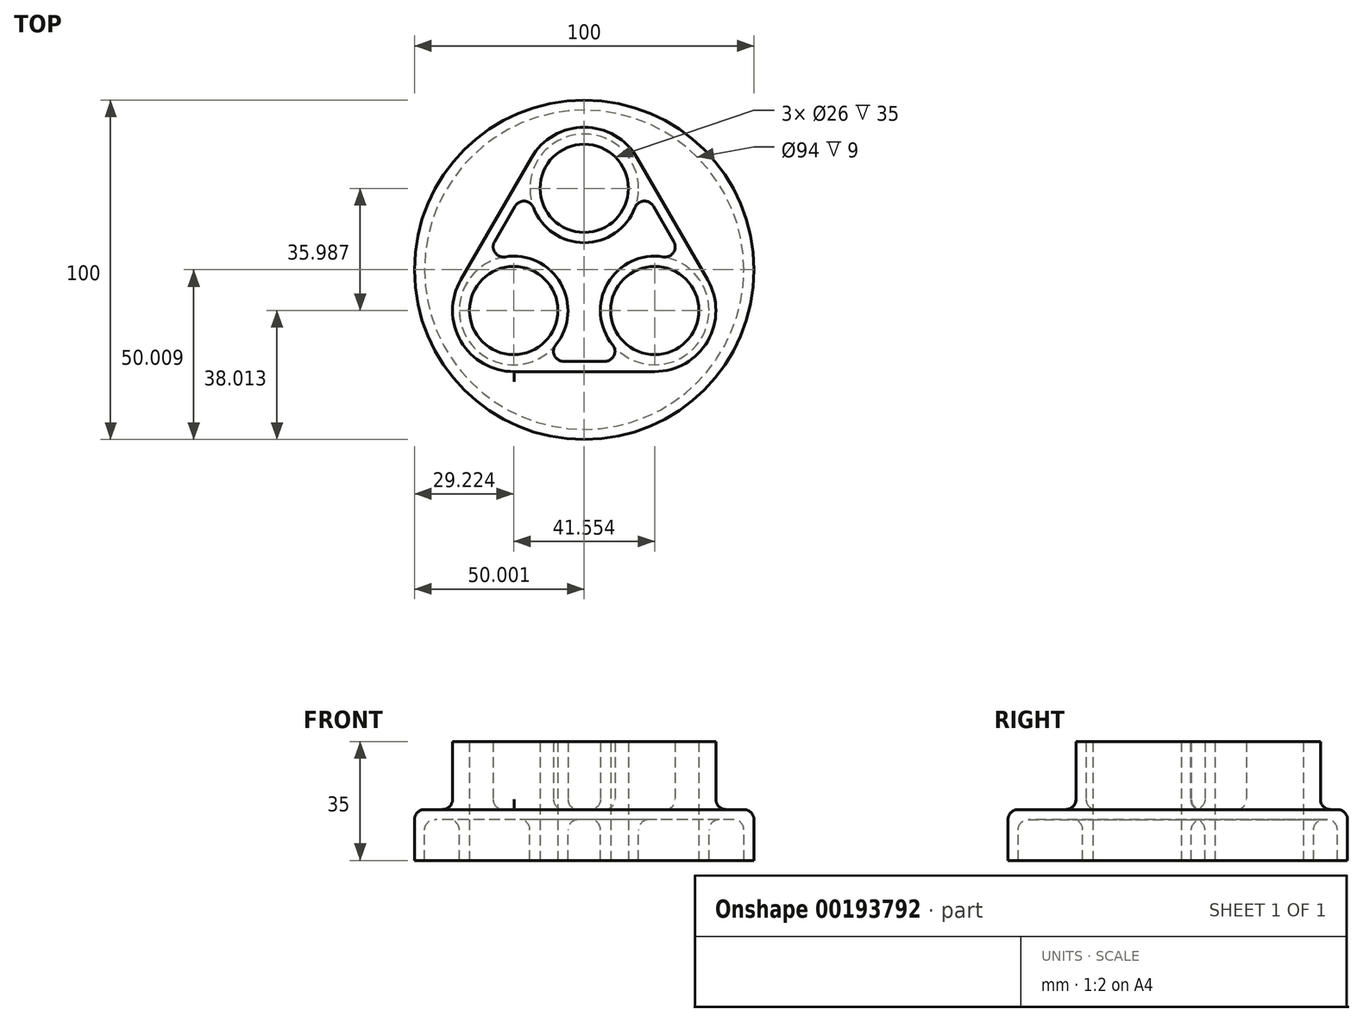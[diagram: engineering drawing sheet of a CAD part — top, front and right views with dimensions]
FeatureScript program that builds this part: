
annotation { "Feature Type Name" : "Feature", "Feature Type Description" : "" }
export const myFeature = defineFeature(function(context is Context, id is Id, definition is map)
    precondition{}
    {
        {
            var Q0;
            Q0=qCreatedBy(makeId("Top.planeOp"),FACE);
            var sketch = newSketch(context, id + "F0", { "sketchPlane" : qUnion([Q0])});
            skCircle(sketch, "E0", {"center": v(0, 0) * mm, "radius": 24 * mm, "construction": true});
            skCircle(sketch, "E1", {"center": v(0, 24) * mm, "radius": 13 * mm});
            skCircle(sketch, "E2", {"center": v(0, 24) * mm, "radius": 18 * mm});
            skCircle(sketch, "E3.1.0", {"center": v(-20.78, -11.99) * mm, "radius": 18 * mm});
            skCircle(sketch, "E3.1.1", {"center": v(-20.78, -11.99) * mm, "radius": 13 * mm});
            skCircle(sketch, "E3.2.0", {"center": v(20.78, -11.99) * mm, "radius": 18 * mm});
            skCircle(sketch, "E3.2.1", {"center": v(20.78, -11.99) * mm, "radius": 13 * mm});
            skCircle(sketch, "E4", {"center": v(0, 0) * mm, "radius": 50 * mm});
            skLineSegment(sketch, "E5", {"start": v(-15.59, 33) * mm, "end": v(-36.36, -2.99) * mm});
            skLineSegment(sketch, "E6", {"start": v(15.59, 33) * mm, "end": v(36.37, -2.99) * mm});
            skLineSegment(sketch, "E7", {"start": v(-15.2, -26.99) * mm, "end": v(15.2, -26.99) * mm});
            skLineSegment(sketch, "E8", {"start": v(30.98, 0.34) * mm, "end": v(15.77, 26.68) * mm});
            skLineSegment(sketch, "E9", {"start": v(-15.77, 26.68) * mm, "end": v(-30.98, 0.33) * mm});
            skLineSegment(sketch, "E10", {"start": v(-20.6, -29.99) * mm, "end": v(20.78, -29.99) * mm});
            skCircle(sketch, "E11", {"center": v(0, 24) * mm, "radius": 16 * mm});
            skCircle(sketch, "E12", {"center": v(20.78, -11.99) * mm, "radius": 16 * mm});
            skCircle(sketch, "E13", {"center": v(-20.78, -11.99) * mm, "radius": 16 * mm});
            skCircle(sketch, "E14", {"center": v(0, 0) * mm, "radius": 47 * mm});
            skSolve(sketch);
        }
        {
            var Q0;
            {var subQ0=sQuery(id+"F0.wireOp",EDGE,"E7");Q0=makeQuery(id+"F0.imprint","IMPRINT",FACE,{"disambiguationData":[TD([[makeQuery(id+"F0.imprint","IMPRINT",EDGE,{"derivedFrom":subQ0}),-1.0]])]});}
            var Q1;
            Q1=makeQuery(id+"F0.imprint","IMPRINT",FACE,{"disambiguationData":[TD([[makeQuery(id+"F0.imprint","IMPRINT",EDGE,{"derivedFrom":sQuery(id+"F0.wireOp",EDGE,"E3.2.1")}),-1.0]])]});
            var Q2;
            Q2=makeQuery(id+"F0.imprint","IMPRINT",FACE,{"disambiguationData":[TD([[makeQuery(id+"F0.imprint","IMPRINT",EDGE,{"derivedFrom":sQuery(id+"F0.wireOp",EDGE,"E3.1.1")}),-1.0]])]});
            var Q3;
            Q3=makeQuery(id+"F0.imprint","IMPRINT",FACE,{"disambiguationData":[TD([[makeQuery(id+"F0.imprint","IMPRINT",EDGE,{"derivedFrom":sQuery(id+"F0.wireOp",EDGE,"E1")}),-1.0]])]});
            var Q4;
            {var subQ0=sQuery(id+"F0.wireOp",EDGE,"E6");Q4=makeQuery(id+"F0.imprint","IMPRINT",FACE,{"disambiguationData":[TD([[makeQuery(id+"F0.imprint","IMPRINT",EDGE,{"derivedFrom":subQ0}),-1.0]])]});}
            var Q5;
            {var subQ0=sQuery(id+"F0.wireOp",EDGE,"E5");Q5=makeQuery(id+"F0.imprint","IMPRINT",FACE,{"disambiguationData":[TD([[makeQuery(id+"F0.imprint","IMPRINT",EDGE,{"derivedFrom":subQ0}),1.0]])]});}
            var Q6;
            {var subQ3=sQuery(id+"F0.wireOp",EDGE,"E3.1.0");var subQ5=makeQuery(id+"F0.imprint","INTERSECT",VERTEX,{"derivedFrom":[subQ3,sQuery(id+"F0.wireOp",EDGE,"E5")]});Q6=makeQuery(id+"F0.imprint","IMPRINT",FACE,{"disambiguationData":[TD([[makeQuery(id+"F0.imprint","IMPRINT",EDGE,{"disambiguationData":[TD([[subQ5,-1.0]])],"derivedFrom":subQ3}),1.0]])]});}
            var Q7;
            {var subQ0=sQuery(id+"F0.wireOp",EDGE,"E2");var subQ6=makeQuery(id+"F0.imprint","INTERSECT",VERTEX,{"derivedFrom":[subQ0,sQuery(id+"F0.wireOp",EDGE,"E5")]});Q7=makeQuery(id+"F0.imprint","IMPRINT",FACE,{"disambiguationData":[TD([[makeQuery(id+"F0.imprint","IMPRINT",EDGE,{"disambiguationData":[TD([[subQ6,1.0]])],"derivedFrom":subQ0}),1.0]])]});}
            var Q8;
            {var subQ3=sQuery(id+"F0.wireOp",EDGE,"E3.2.0");var subQ8=makeQuery(id+"F0.imprint","INTERSECT",VERTEX,{"derivedFrom":[subQ3,sQuery(id+"F0.wireOp",EDGE,"E6")]});Q8=makeQuery(id+"F0.imprint","IMPRINT",FACE,{"disambiguationData":[TD([[makeQuery(id+"F0.imprint","IMPRINT",EDGE,{"disambiguationData":[TD([[subQ8,1.0]])],"derivedFrom":subQ3}),1.0]])]});}
            extrude(context, id + "F1", {"entities" : qUnion([Q0, Q1, Q2, Q3, Q4, Q5, Q6, Q7, Q8]), "depth" : 20 * mm});
        }
        {
            var Q0;
            Q0=makeQuery(id+"F0.imprint","IMPRINT",FACE,{"disambiguationData":[TD([[makeQuery(id+"F0.imprint","IMPRINT",EDGE,{"derivedFrom":sQuery(id+"F0.wireOp",EDGE,"E4")}),1.0]])]});
            var Q1;
            {var subQ7=sQuery(id+"F0.wireOp",EDGE,"E9");var subQ9=sQuery(id+"F0.wireOp",EDGE,"E2");var subQ10=makeQuery(id+"F0.imprint","INTERSECT",VERTEX,{"derivedFrom":[subQ9,subQ7]});Q1=makeQuery(id+"F0.imprint","IMPRINT",FACE,{"disambiguationData":[TD([[makeQuery(id+"F0.imprint","IMPRINT",EDGE,{"disambiguationData":[TD([[subQ10,-1.0]])],"derivedFrom":subQ9}),-1.0]])]});}
            var Q2;
            {var subQ0=sQuery(id+"F0.wireOp",EDGE,"E8");var subQ1=sQuery(id+"F0.wireOp",EDGE,"E3.2.0");var subQ2=makeQuery(id+"F0.imprint","INTERSECT",VERTEX,{"derivedFrom":[subQ1,subQ0]});Q2=makeQuery(id+"F0.imprint","IMPRINT",FACE,{"disambiguationData":[TD([[makeQuery(id+"F0.imprint","IMPRINT",EDGE,{"disambiguationData":[TD([[subQ2,-1.0]])],"derivedFrom":subQ1}),1.0]])]});}
            var Q3;
            {var subQ0=sQuery(id+"F0.wireOp",EDGE,"E7");var subQ1=sQuery(id+"F0.wireOp",EDGE,"E3.1.0");var subQ2=makeQuery(id+"F0.imprint","INTERSECT",VERTEX,{"derivedFrom":[subQ1,subQ0]});Q3=makeQuery(id+"F0.imprint","IMPRINT",FACE,{"disambiguationData":[TD([[makeQuery(id+"F0.imprint","IMPRINT",EDGE,{"disambiguationData":[TD([[subQ2,-1.0]])],"derivedFrom":subQ1}),1.0]])]});}
            var Q4;
            Q4=makeQuery(id+"F0.imprint","IMPRINT",FACE,{"disambiguationData":[TD([[makeQuery(id+"F0.imprint","IMPRINT",EDGE,{"derivedFrom":sQuery(id+"F0.wireOp",EDGE,"E1")}),-1.0]])]});
            var Q5;
            {var subQ0=sQuery(id+"F0.wireOp",EDGE,"E9");var subQ1=sQuery(id+"F0.wireOp",EDGE,"E2");var subQ2=makeQuery(id+"F0.imprint","INTERSECT",VERTEX,{"derivedFrom":[subQ1,subQ0]});Q5=makeQuery(id+"F0.imprint","IMPRINT",FACE,{"disambiguationData":[TD([[makeQuery(id+"F0.imprint","IMPRINT",EDGE,{"disambiguationData":[TD([[subQ2,-1.0]])],"derivedFrom":subQ1}),1.0]])]});}
            var Q6;
            {var subQ0=sQuery(id+"F0.wireOp",EDGE,"E5");Q6=makeQuery(id+"F0.imprint","IMPRINT",FACE,{"disambiguationData":[TD([[makeQuery(id+"F0.imprint","IMPRINT",EDGE,{"derivedFrom":subQ0}),1.0]])]});}
            var Q7;
            Q7=makeQuery(id+"F0.imprint","IMPRINT",FACE,{"disambiguationData":[TD([[makeQuery(id+"F0.imprint","IMPRINT",EDGE,{"derivedFrom":sQuery(id+"F0.wireOp",EDGE,"E3.1.1")}),-1.0]])]});
            var Q8;
            {var subQ3=sQuery(id+"F0.wireOp",EDGE,"E3.1.0");var subQ5=makeQuery(id+"F0.imprint","INTERSECT",VERTEX,{"derivedFrom":[subQ3,sQuery(id+"F0.wireOp",EDGE,"E5")]});Q8=makeQuery(id+"F0.imprint","IMPRINT",FACE,{"disambiguationData":[TD([[makeQuery(id+"F0.imprint","IMPRINT",EDGE,{"disambiguationData":[TD([[subQ5,-1.0]])],"derivedFrom":subQ3}),1.0]])]});}
            var Q9;
            Q9=makeQuery(id+"F0.imprint","IMPRINT",FACE,{"disambiguationData":[TD([[makeQuery(id+"F0.imprint","IMPRINT",EDGE,{"derivedFrom":sQuery(id+"F0.wireOp",EDGE,"E3.2.1")}),-1.0]])]});
            var Q10;
            {var subQ0=sQuery(id+"F0.wireOp",EDGE,"E10");Q10=makeQuery(id+"F0.imprint","IMPRINT",FACE,{"disambiguationData":[TD([[makeQuery(id+"F0.imprint","IMPRINT",EDGE,{"derivedFrom":subQ0}),1.0]])]});}
            var Q11;
            {var subQ3=sQuery(id+"F0.wireOp",EDGE,"E3.2.0");var subQ8=makeQuery(id+"F0.imprint","INTERSECT",VERTEX,{"derivedFrom":[subQ3,sQuery(id+"F0.wireOp",EDGE,"E6")]});Q11=makeQuery(id+"F0.imprint","IMPRINT",FACE,{"disambiguationData":[TD([[makeQuery(id+"F0.imprint","IMPRINT",EDGE,{"disambiguationData":[TD([[subQ8,1.0]])],"derivedFrom":subQ3}),1.0]])]});}
            var Q12;
            {var subQ0=sQuery(id+"F0.wireOp",EDGE,"E6");Q12=makeQuery(id+"F0.imprint","IMPRINT",FACE,{"disambiguationData":[TD([[makeQuery(id+"F0.imprint","IMPRINT",EDGE,{"derivedFrom":subQ0}),-1.0]])]});}
            var Q13;
            {var subQ0=sQuery(id+"F0.wireOp",EDGE,"E2");var subQ6=makeQuery(id+"F0.imprint","INTERSECT",VERTEX,{"derivedFrom":[subQ0,sQuery(id+"F0.wireOp",EDGE,"E5")]});Q13=makeQuery(id+"F0.imprint","IMPRINT",FACE,{"disambiguationData":[TD([[makeQuery(id+"F0.imprint","IMPRINT",EDGE,{"disambiguationData":[TD([[subQ6,1.0]])],"derivedFrom":subQ0}),1.0]])]});}
            var Q14;
            {var subQ3=sQuery(id+"F0.wireOp",EDGE,"E5");Q14=makeQuery(id+"F0.imprint","IMPRINT",FACE,{"disambiguationData":[TD([[makeQuery(id+"F0.imprint","IMPRINT",EDGE,{"derivedFrom":subQ3}),-1.0]])]});}
            extrude(context, id + "F2", {"entities" : qUnion([Q0, Q1, Q2, Q3, Q4, Q5, Q6, Q7, Q8, Q9, Q10, Q11, Q12, Q13, Q14]), "operationType" : NewBodyOperationType.ADD, "oppositeDirection" : true, "depth" : 3 * mm});
        }
        {
            var Q0;
            Q0=makeQuery(id+"F0.imprint","IMPRINT",FACE,{"disambiguationData":[TD([[makeQuery(id+"F0.imprint","IMPRINT",EDGE,{"derivedFrom":sQuery(id+"F0.wireOp",EDGE,"E4")}),1.0]])]});
            var Q1;
            Q1=makeQuery(id+"F0.imprint","IMPRINT",FACE,{"disambiguationData":[TD([[makeQuery(id+"F0.imprint","IMPRINT",EDGE,{"derivedFrom":sQuery(id+"F0.wireOp",EDGE,"E3.1.1")}),-1.0]])]});
            var Q2;
            Q2=makeQuery(id+"F0.imprint","IMPRINT",FACE,{"disambiguationData":[TD([[makeQuery(id+"F0.imprint","IMPRINT",EDGE,{"derivedFrom":sQuery(id+"F0.wireOp",EDGE,"E1")}),-1.0]])]});
            var Q3;
            Q3=makeQuery(id+"F0.imprint","IMPRINT",FACE,{"disambiguationData":[TD([[makeQuery(id+"F0.imprint","IMPRINT",EDGE,{"derivedFrom":sQuery(id+"F0.wireOp",EDGE,"E3.2.1")}),-1.0]])]});
            extrude(context, id + "F3", {"entities" : qUnion([Q0, Q1, Q2, Q3]), "operationType" : NewBodyOperationType.ADD, "oppositeDirection" : true, "depth" : 15 * mm});
        }
        {
            var Q0;
            Q0=makeQuery(id+"F2.boolean.opBoolean","SPLIT",FACE,{"disambiguationData":[TD([makeQuery(id+"F1.opExtrude","SWEPT_FACE",FACE,{"disambiguationData":[OSD([sQuery(id+"F0.wireOp",EDGE,"E7")])]})])],"derivedFrom":makeQuery(id+"F2.opExtrude","CAP_FACE",FACE,{"disambiguationData":[OSD([sQuery(id+"F0.wireOp",EDGE,"E1"),sQuery(id+"F0.wireOp",EDGE,"E3.1.1"),sQuery(id+"F0.wireOp",EDGE,"E3.2.1"),sQuery(id+"F0.wireOp",EDGE,"E4")])],"isStart":true})});
            var Q1;
            Q1=makeQuery(id+"F1.opExtrude","SWEPT_EDGE",EDGE,{"disambiguationData":[OSD([sQuery(id+"F0.wireOp",EDGE,"E8"),sQuery(id+"F0.wireOp",EDGE,"E11")])]});
            var Q2;
            Q2=makeQuery(id+"F1.opExtrude","SWEPT_EDGE",EDGE,{"disambiguationData":[OSD([sQuery(id+"F0.wireOp",EDGE,"E9"),sQuery(id+"F0.wireOp",EDGE,"E11")])]});
            var Q3;
            Q3=makeQuery(id+"F1.opExtrude","SWEPT_EDGE",EDGE,{"disambiguationData":[OSD([sQuery(id+"F0.wireOp",EDGE,"E9"),sQuery(id+"F0.wireOp",EDGE,"E13")])]});
            var Q4;
            Q4=makeQuery(id+"F1.opExtrude","SWEPT_EDGE",EDGE,{"disambiguationData":[OSD([sQuery(id+"F0.wireOp",EDGE,"E7"),sQuery(id+"F0.wireOp",EDGE,"E13")])]});
            var Q5;
            Q5=makeQuery(id+"F1.opExtrude","SWEPT_EDGE",EDGE,{"disambiguationData":[OSD([sQuery(id+"F0.wireOp",EDGE,"E7"),sQuery(id+"F0.wireOp",EDGE,"E12")])]});
            var Q6;
            Q6=makeQuery(id+"F1.opExtrude","SWEPT_EDGE",EDGE,{"disambiguationData":[OSD([sQuery(id+"F0.wireOp",EDGE,"E8"),sQuery(id+"F0.wireOp",EDGE,"E12")])]});
            var Q7;
            {var subQ0=sQuery(id+"F0.wireOp",EDGE,"E4");Q7=makeQuery(id+"F2.boolean.opBoolean","SPLIT",FACE,{"disambiguationData":[TD([makeQuery(id+"F1.opExtrude","SWEPT_FACE",FACE,{"disambiguationData":[OSD([sQuery(id+"F0.wireOp",EDGE,"E2")])]})])],"derivedFrom":makeQuery(id+"F2.opExtrude","CAP_FACE",FACE,{"disambiguationData":[OSD([sQuery(id+"F0.wireOp",EDGE,"E1"),sQuery(id+"F0.wireOp",EDGE,"E3.1.1"),sQuery(id+"F0.wireOp",EDGE,"E3.2.1"),subQ0])],"isStart":true})});}
            var Q8;
            Q8=makeQuery(id+"F2.opExtrude","CAP_FACE",FACE,{"disambiguationData":[OSD([sQuery(id+"F0.wireOp",EDGE,"E1"),sQuery(id+"F0.wireOp",EDGE,"E3.1.1"),sQuery(id+"F0.wireOp",EDGE,"E3.2.1"),sQuery(id+"F0.wireOp",EDGE,"E4")])],"isStart":false});
            fillet(context, id + "F4", {"entities" : qUnion([Q0, Q1, Q2, Q3, Q4, Q5, Q6, Q7, Q8]), "radius" : 3 * mm, "tangentPropagation" : true, "allowEdgeOverflow" : false});
        }
    });
